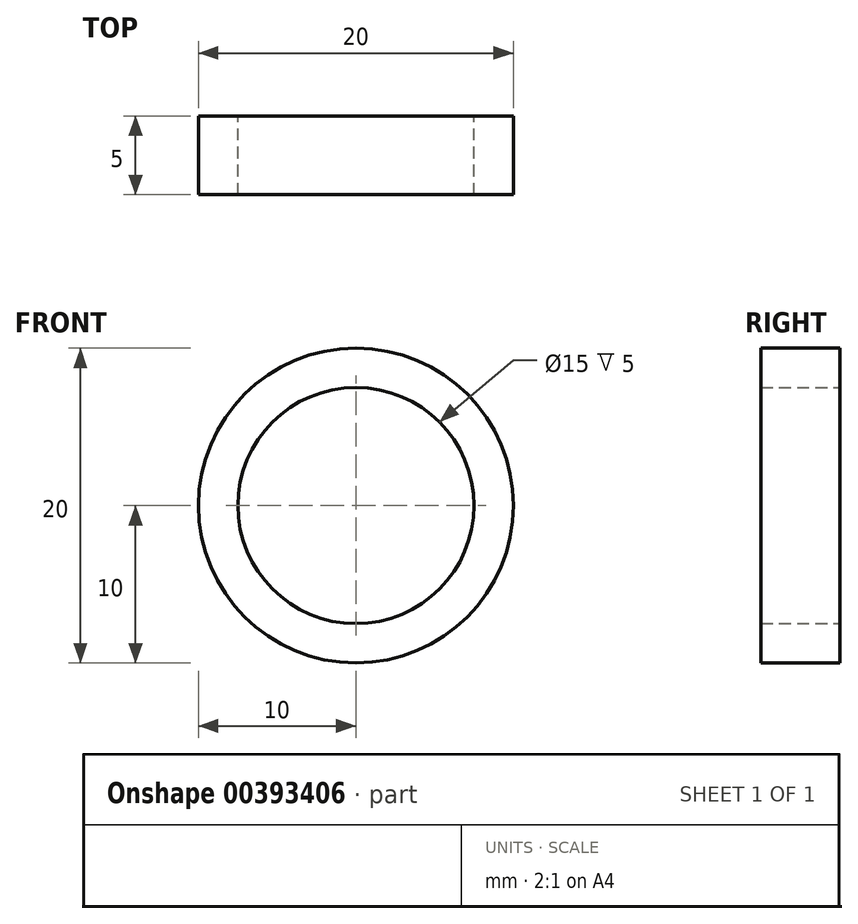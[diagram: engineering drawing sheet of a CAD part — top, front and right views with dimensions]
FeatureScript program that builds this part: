
annotation { "Feature Type Name" : "Feature", "Feature Type Description" : "" }
export const myFeature = defineFeature(function(context is Context, id is Id, definition is map)
    precondition{}
    {
        {
            var Q0;
            Q0=qCreatedBy(makeId("Front.planeOp"),FACE);
            var sketch = newSketch(context, id + "F0", { "sketchPlane" : qUnion([Q0])});
            skCircle(sketch, "E0", {"center": v(0, 0) * mm, "radius": 10 * mm});
            skCircle(sketch, "E1", {"center": v(0, 0) * mm, "radius": 7.5 * mm});
            skSolve(sketch);
        }
        {
            var Q0;
            Q0=makeQuery(id+"F0.imprint","IMPRINT",FACE,{"disambiguationData":[TD([[makeQuery(id+"F0.imprint","IMPRINT",EDGE,{"derivedFrom":sQuery(id+"F0.wireOp",EDGE,"E0")}),1.0]])]});
            var Q1;
            Q1=sQuery(id+"F0.wireOp",EDGE,"E0");
            extrude(context, id + "F1", {"entities" : qUnion([Q0]), "surfaceEntities" : qUnion([Q1]), "depth" : 5 * mm});
        }
    });
